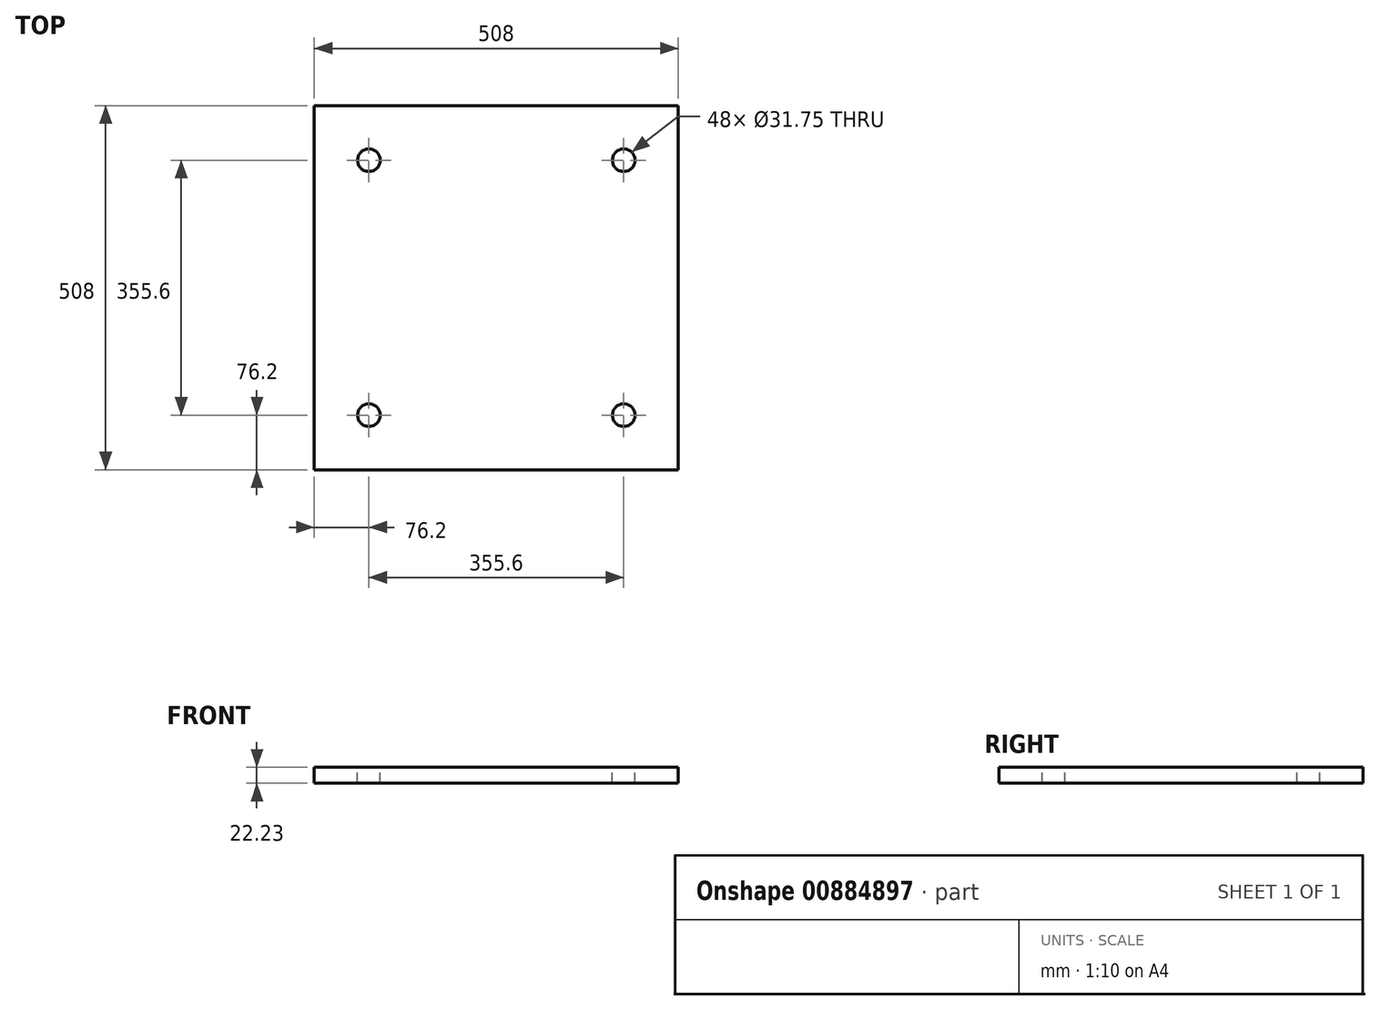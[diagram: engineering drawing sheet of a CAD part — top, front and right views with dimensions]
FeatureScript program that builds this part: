
annotation { "Feature Type Name" : "Feature", "Feature Type Description" : "" }
export const myFeature = defineFeature(function(context is Context, id is Id, definition is map)
    precondition{}
    {
        {
            var Q0;
            Q0=qCreatedBy(makeId("Top.planeOp"),FACE);
            var sketch = newSketch(context, id + "F0", { "sketchPlane" : qUnion([Q0])});
            skLineSegment(sketch, "E0.bottom", {"start": v(-254, 254) * mm, "end": v(254, 254) * mm});
            skLineSegment(sketch, "E0.top", {"start": v(-254, -254) * mm, "end": v(254, -254) * mm});
            skLineSegment(sketch, "E0.left", {"start": v(-254, 254) * mm, "end": v(-254, -254) * mm});
            skLineSegment(sketch, "E0.right", {"start": v(254, 254) * mm, "end": v(254, -254) * mm});
            skSolve(sketch);
        }
        {
            var Q0;
            Q0=qSketchRegion(id+"F0",true);
            extrude(context, id + "F1", {"entities" : qUnion([Q0]), "depth" : 22.22 * mm, "offsetDistance" : 25.4 * mm});
        }
        {
            var Q0;
            Q0=makeQuery(id+"F1.opExtrude","CAP_FACE",FACE,{"disambiguationData":[OSD([sQuery(id+"F0.wireOp",EDGE,"E0.bottom"),sQuery(id+"F0.wireOp",EDGE,"E0.top"),sQuery(id+"F0.wireOp",EDGE,"E0.left"),sQuery(id+"F0.wireOp",EDGE,"E0.right")])],"isStart":false});
            var sketch = newSketch(context, id + "F2", { "sketchPlane" : qUnion([Q0])});
            skCircle(sketch, "E1", {"center": v(-177.8, 177.8) * mm, "radius": 12.7 * mm});
            skCircle(sketch, "E2.1.0.0", {"center": v(177.8, 177.8) * mm, "radius": 12.7 * mm});
            skLineSegment(sketch, "E2.direction1", {"start": v(-177.8, 177.8) * mm, "end": v(177.8, 177.8) * mm, "construction": true});
            skCircle(sketch, "E3.0.1.0", {"center": v(-177.8, -177.8) * mm, "radius": 12.7 * mm});
            skCircle(sketch, "E3.1.1.0", {"center": v(177.8, -177.8) * mm, "radius": 12.7 * mm});
            skLineSegment(sketch, "E3.direction2", {"start": v(-177.8, 177.8) * mm, "end": v(-177.8, -177.8) * mm, "construction": true});
            skSolve(sketch);
        }
        {
            var Q0;
            Q0=sQuery(id+"F2.wireOp",VERTEX,"E3.direction2.end");
            var Q1;
            Q1=sQuery(id+"F2.wireOp",VERTEX,"E2.direction1.start");
            var Q2;
            Q2=sQuery(id+"F2.wireOp",VERTEX,"E2.direction1.end");
            var Q3;
            Q3=sQuery(id+"F2.wireOp",VERTEX,"E3.1.1.0.center");
            var Q4;
            Q4=makeQuery(id+"F1.opExtrude","SWEPT_BODY",BODY,{"disambiguationData":[OSD([sQuery(id+"F0.wireOp",EDGE,"E0.bottom"),sQuery(id+"F0.wireOp",EDGE,"E0.top"),sQuery(id+"F0.wireOp",EDGE,"E0.left"),sQuery(id+"F0.wireOp",EDGE,"E0.right")])]});
            hole(context, id + "F3", {"style" : HoleStyle.SIMPLE, "endStyle" : HoleEndStyle.THROUGH, "holeDiameter" : 31.75 * mm, "majorDiameter" : 6.35 * mm, "isTappedThrough" : true, "tappedDepth" : 12.7 * mm, "tapClearance" : 3, "locations" : qUnion([Q0, Q1, Q2, Q3]), "scope" : qUnion([Q4])});
        }
    });
